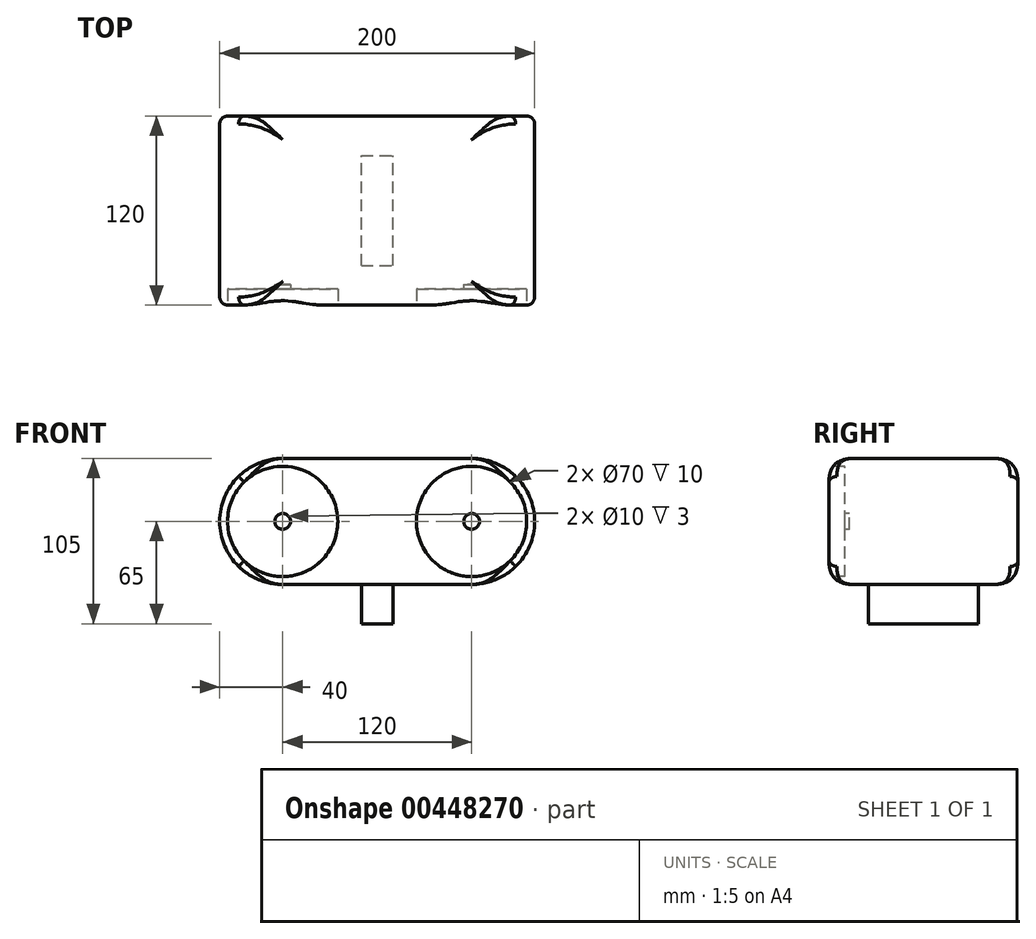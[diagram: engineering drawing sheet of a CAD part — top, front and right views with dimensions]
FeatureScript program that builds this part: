
annotation { "Feature Type Name" : "Feature", "Feature Type Description" : "" }
export const myFeature = defineFeature(function(context is Context, id is Id, definition is map)
    precondition{}
    {
        {
            var Q0;
            Q0=qCreatedBy(makeId("Front.planeOp"),FACE);
            var sketch = newSketch(context, id + "F0", { "sketchPlane" : qUnion([Q0])});
            skArc(sketch, "E0", {"start": v(-60, 60) * mm, "mid": v(-100, 20) * mm, "end": v(-60, -20) * mm});
            skArc(sketch, "E1", {"start": v(60, -20) * mm, "mid": v(100, 20) * mm, "end": v(60, 60) * mm});
            skLineSegment(sketch, "E2", {"start": v(-60, 60) * mm, "end": v(60, 60) * mm});
            skLineSegment(sketch, "E3", {"start": v(-60, -20) * mm, "end": v(60, -20) * mm});
            skSolve(sketch);
        }
        {
            var Q0;
            Q0=makeQuery(id+"F0.imprint","IMPRINT",FACE,{"disambiguationData":[TD([[makeQuery(id+"F0.imprint","IMPRINT",EDGE,{"derivedFrom":sQuery(id+"F0.wireOp",EDGE,"E0")}),1.0]])]});
            extrude(context, id + "F1", {"entities" : qUnion([Q0]), "depth" : 120 * mm});
        }
        {
            var Q0;
            Q0=makeQuery(id+"F1.opExtrude","CAP_FACE",FACE,{"disambiguationData":[OSD([sQuery(id+"F0.wireOp",EDGE,"E0"),sQuery(id+"F0.wireOp",EDGE,"E1"),sQuery(id+"F0.wireOp",EDGE,"E2"),sQuery(id+"F0.wireOp",EDGE,"E3")])],"isStart":false});
            var sketch = newSketch(context, id + "F2", { "sketchPlane" : qUnion([Q0])});
            skCircle(sketch, "E4", {"center": v(-60, 20) * mm, "radius": 35 * mm});
            skCircle(sketch, "E5", {"center": v(60, 20) * mm, "radius": 35 * mm});
            skSolve(sketch);
        }
        {
            var Q0;
            Q0=makeQuery(id+"F2.imprint","IMPRINT",FACE,{"disambiguationData":[TD([[makeQuery(id+"F2.imprint","IMPRINT",EDGE,{"derivedFrom":sQuery(id+"F2.wireOp",EDGE,"E4")}),1.0]])]});
            var Q1;
            Q1=makeQuery(id+"F2.imprint","IMPRINT",FACE,{"disambiguationData":[TD([[makeQuery(id+"F2.imprint","IMPRINT",EDGE,{"derivedFrom":sQuery(id+"F2.wireOp",EDGE,"E5")}),1.0]])]});
            extrude(context, id + "F3", {"entities" : qUnion([Q0, Q1]), "operationType" : NewBodyOperationType.REMOVE, "oppositeDirection" : true, "depth" : 10 * mm});
        }
        {
            var Q0;
            Q0=makeQuery(id+"F1.opExtrude","SWEPT_FACE",FACE,{"disambiguationData":[OSD([sQuery(id+"F0.wireOp",EDGE,"E3")])]});
            var sketch = newSketch(context, id + "F4", { "sketchPlane" : qUnion([Q0])});
            skLineSegment(sketch, "E6.bottom", {"start": v(-10, 95) * mm, "end": v(10, 95) * mm});
            skLineSegment(sketch, "E6.top", {"start": v(-10, 25) * mm, "end": v(10, 25) * mm});
            skLineSegment(sketch, "E6.left", {"start": v(-10, 95) * mm, "end": v(-10, 25) * mm});
            skLineSegment(sketch, "E6.right", {"start": v(10, 95) * mm, "end": v(10, 25) * mm});
            skSolve(sketch);
        }
        {
            var Q0;
            Q0=makeQuery(id+"F4.imprint","IMPRINT",FACE,{"disambiguationData":[TD([[makeQuery(id+"F4.imprint","IMPRINT",EDGE,{"derivedFrom":sQuery(id+"F4.wireOp",EDGE,"E6.bottom")}),-1.0]])]});
            extrude(context, id + "F5", {"entities" : qUnion([Q0]), "operationType" : NewBodyOperationType.ADD, "depth" : 25 * mm});
        }
        {
            var Q0;
            Q0=makeQuery(id+"F3.boolean.opBoolean","COPY",FACE,{"derivedFrom":makeQuery(id+"F3.opExtrude","CAP_FACE",FACE,{"disambiguationData":[OSD([sQuery(id+"F2.wireOp",EDGE,"E4")])],"isStart":false})});
            var sketch = newSketch(context, id + "F6", { "sketchPlane" : qUnion([Q0])});
            skCircle(sketch, "E7", {"center": v(-60, 20) * mm, "radius": 5 * mm});
            skCircle(sketch, "E8", {"center": v(60, 20) * mm, "radius": 5 * mm});
            skSolve(sketch);
        }
        {
            var Q0;
            Q0=makeQuery(id+"F6.imprint","IMPRINT",FACE,{"disambiguationData":[TD([[makeQuery(id+"F6.imprint","IMPRINT",EDGE,{"derivedFrom":sQuery(id+"F6.wireOp",EDGE,"E7")}),1.0]])]});
            var Q1;
            Q1=makeQuery(id+"F6.imprint","IMPRINT",FACE,{"disambiguationData":[TD([[makeQuery(id+"F6.imprint","IMPRINT",EDGE,{"derivedFrom":sQuery(id+"F6.wireOp",EDGE,"E8")}),1.0]])]});
            extrude(context, id + "F7", {"entities" : qUnion([Q0, Q1]), "operationType" : NewBodyOperationType.REMOVE, "oppositeDirection" : true, "depth" : 3 * mm});
        }
        {
            var Q0;
            Q0=makeQuery(id+"F5.opExtrude","SWEPT_FACE",FACE,{"disambiguationData":[OSD([sQuery(id+"F4.wireOp",EDGE,"E6.right")])]});
            cPlane(context, id + "F8", {"entities" : qUnion([Q0]), "cplaneType" : CPlaneType.OFFSET, "offset" : 93.3 * mm, "width" : 150 * mm, "height" : 150 * mm});
        }
        {
            var Q0;
            Q0=qCreatedBy(id+"F8.planeOp",FACE);
            var sketch = newSketch(context, id + "F9", { "sketchPlane" : qUnion([Q0])});
            skLineSegment(sketch, "E9", {"start": v(-108.6, 60) * mm, "end": v(40.01, 60) * mm, "construction": true});
            skLineSegment(sketch, "E10", {"start": v(-108.6, -20) * mm, "end": v(40.01, -20) * mm, "construction": true});
            skLineSegment(sketch, "E11", {"start": v(-120, 60.12) * mm, "end": v(-120, -35.35) * mm, "construction": true});
            skLineSegment(sketch, "E12", {"start": v(0, 61.4) * mm, "end": v(0, -35.56) * mm, "construction": true});
            skLineSegment(sketch, "E13", {"start": v(-115, 58.42) * mm, "end": v(-115, -21.96) * mm, "construction": true});
            skLineSegment(sketch, "E14", {"start": v(-106.7, 55) * mm, "end": v(43.75, 55) * mm, "construction": true});
            skLineSegment(sketch, "E15", {"start": v(-105, 57.53) * mm, "end": v(-105, -28.1) * mm, "construction": true});
            skLineSegment(sketch, "E16", {"start": v(-106.7, 45) * mm, "end": v(42.4, 45) * mm, "construction": true});
            skFitSpline(sketch, "E17", {"points": [v(-105, 60) * mm, v(-120, 45) * mm], "startDerivative": vector(-30, 0) * mm, "endDerivative": vector(0, -30) * mm});
            skLineSegment(sketch, "E18", {"start": v(-112.83, -15) * mm, "end": v(39.4, -15) * mm, "construction": true});
            skLineSegment(sketch, "E19", {"start": v(-112.08, -5) * mm, "end": v(40.45, -5) * mm, "construction": true});
            skLineSegment(sketch, "E20", {"start": v(-5, 61.42) * mm, "end": v(-5, -28.1) * mm, "construction": true});
            skLineSegment(sketch, "E21", {"start": v(-15, 58.9) * mm, "end": v(-15, -30.82) * mm, "construction": true});
            skFitSpline(sketch, "E22", {"points": [v(-15, 60) * mm, v(0, 45) * mm], "startDerivative": vector(30, 0) * mm, "endDerivative": vector(0, -30) * mm});
            skFitSpline(sketch, "E23", {"points": [v(-120, -5) * mm, v(-105, -20) * mm], "startDerivative": vector(0, -30) * mm, "endDerivative": vector(30, 0) * mm});
            skFitSpline(sketch, "E24", {"points": [v(0, -5) * mm, v(-15, -20) * mm], "startDerivative": vector(0, -30) * mm, "endDerivative": vector(-30, 0) * mm});
            skLineSegment(sketch, "E25", {"start": v(-105, 60) * mm, "end": v(-120, 60) * mm});
            skLineSegment(sketch, "E26", {"start": v(-120, 45) * mm, "end": v(-120, 60) * mm});
            skLineSegment(sketch, "E27", {"start": v(-120, -5) * mm, "end": v(-120, -20) * mm});
            skLineSegment(sketch, "E28", {"start": v(-120, -20) * mm, "end": v(-105, -20) * mm});
            skLineSegment(sketch, "E29", {"start": v(-15, -20) * mm, "end": v(0, -20) * mm});
            skLineSegment(sketch, "E30", {"start": v(0, -20) * mm, "end": v(0, -5) * mm});
            skLineSegment(sketch, "E31", {"start": v(0, 45) * mm, "end": v(0, 60) * mm});
            skLineSegment(sketch, "E32", {"start": v(0, 60) * mm, "end": v(-15, 60) * mm});
            skSolve(sketch);
        }
        {
            var Q0;
            Q0=makeQuery(id+"F9.imprint","IMPRINT",FACE,{"disambiguationData":[TD([[makeQuery(id+"F9.imprint","IMPRINT",EDGE,{"derivedFrom":sQuery(id+"F9.wireOp",EDGE,"E17")}),-1.0]])]});
            var Q1;
            Q1=makeQuery(id+"F9.imprint","IMPRINT",FACE,{"disambiguationData":[TD([[makeQuery(id+"F9.imprint","IMPRINT",EDGE,{"derivedFrom":sQuery(id+"F9.wireOp",EDGE,"E22")}),1.0]])]});
            var Q2;
            Q2=makeQuery(id+"F9.imprint","IMPRINT",FACE,{"disambiguationData":[TD([[makeQuery(id+"F9.imprint","IMPRINT",EDGE,{"derivedFrom":sQuery(id+"F9.wireOp",EDGE,"E23")}),-1.0]])]});
            var Q3;
            Q3=makeQuery(id+"F9.imprint","IMPRINT",FACE,{"disambiguationData":[TD([[makeQuery(id+"F9.imprint","IMPRINT",EDGE,{"derivedFrom":sQuery(id+"F9.wireOp",EDGE,"E24")}),1.0]])]});
            extrude(context, id + "F10", {"entities" : qUnion([Q0, Q1, Q2, Q3]), "operationType" : NewBodyOperationType.REMOVE, "oppositeDirection" : true, "depth" : 222 * mm});
        }
        {
            var Q0;
            Q0=makeQuery(id+"F1.opExtrude","CAP_EDGE",EDGE,{"disambiguationData":[OSD([sQuery(id+"F0.wireOp",EDGE,"E0")])],"isStart":false});
            var Q1;
            Q1=makeQuery(id+"F10.boolean.opBoolean","INTERSECT",EDGE,{"derivedFrom":[makeQuery(id+"F1.opExtrude","SWEPT_FACE",FACE,{"disambiguationData":[OSD([sQuery(id+"F0.wireOp",EDGE,"E0")])]}),makeQuery(id+"F10.opExtrude","SWEPT_FACE",FACE,{"disambiguationData":[OSD([sQuery(id+"F9.wireOp",EDGE,"E17")])]})]});
            var Q2;
            Q2=makeQuery(id+"F10.boolean.opBoolean","INTERSECT",EDGE,{"derivedFrom":[makeQuery(id+"F1.opExtrude","SWEPT_FACE",FACE,{"disambiguationData":[OSD([sQuery(id+"F0.wireOp",EDGE,"E0")])]}),makeQuery(id+"F10.opExtrude","SWEPT_FACE",FACE,{"disambiguationData":[OSD([sQuery(id+"F9.wireOp",EDGE,"E23")])]})]});
            var Q3;
            Q3=makeQuery(id+"F1.opExtrude","SWEPT_FACE",FACE,{"disambiguationData":[OSD([sQuery(id+"F0.wireOp",EDGE,"E1")])]});
            var Q4;
            Q4=makeQuery(id+"F1.opExtrude","SWEPT_FACE",FACE,{"disambiguationData":[OSD([sQuery(id+"F0.wireOp",EDGE,"E0")])]});
            var Q5;
            Q5=makeQuery(id+"F1.opExtrude","SWEPT_FACE",FACE,{"disambiguationData":[OSD([sQuery(id+"F0.wireOp",EDGE,"E2")])]});
            fillet(context, id + "F11", {"entities" : qUnion([Q0, Q1, Q2, Q3, Q4, Q5]), "radius" : 5 * mm, "tangentPropagation" : true, "allowEdgeOverflow" : false});
        }
    });
